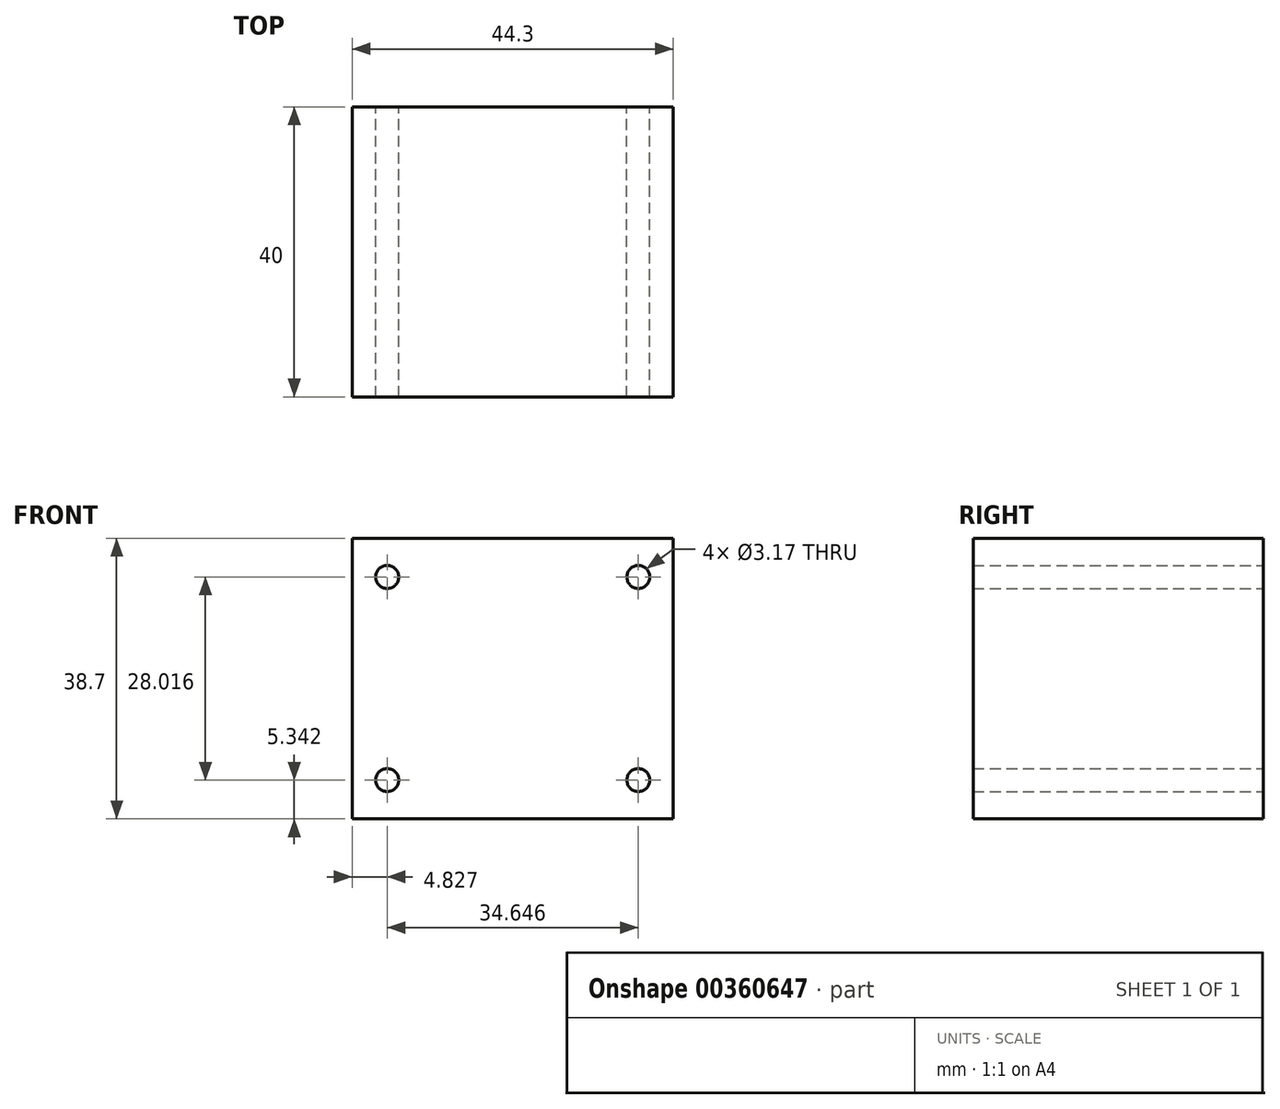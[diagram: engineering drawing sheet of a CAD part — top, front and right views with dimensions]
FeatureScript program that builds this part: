
annotation { "Feature Type Name" : "Feature", "Feature Type Description" : "" }
export const myFeature = defineFeature(function(context is Context, id is Id, definition is map)
    precondition{}
    {
        {
            var Q0;
            Q0=qCreatedBy(makeId("Front.planeOp"),FACE);
            var sketch = newSketch(context, id + "F0", { "sketchPlane" : qUnion([Q0])});
            skLineSegment(sketch, "E0.bottom", {"start": v(-22.15, 19.35) * mm, "end": v(22.15, 19.35) * mm});
            skLineSegment(sketch, "E0.top", {"start": v(-22.15, -19.35) * mm, "end": v(22.15, -19.35) * mm});
            skLineSegment(sketch, "E0.left", {"start": v(-22.15, 19.35) * mm, "end": v(-22.15, -19.35) * mm});
            skLineSegment(sketch, "E0.right", {"start": v(22.15, 19.35) * mm, "end": v(22.15, -19.35) * mm});
            skPoint(sketch, "E1", {"position": v(0, 19.35) * mm});
            skPoint(sketch, "E2", {"position": v(22.15, 0) * mm});
            skLineSegment(sketch, "E3.bottom", {"start": v(-17.32, 14) * mm, "end": v(17.32, 14) * mm, "construction": true});
            skLineSegment(sketch, "E3.top", {"start": v(-17.32, -14) * mm, "end": v(17.32, -14) * mm, "construction": true});
            skLineSegment(sketch, "E3.left", {"start": v(-17.32, 14) * mm, "end": v(-17.32, -14) * mm, "construction": true});
            skLineSegment(sketch, "E3.right", {"start": v(17.32, 14) * mm, "end": v(17.32, -14) * mm, "construction": true});
            skPoint(sketch, "E4", {"position": v(0, 14) * mm});
            skPoint(sketch, "E5", {"position": v(-17.32, 0) * mm});
            skCircle(sketch, "E6", {"center": v(-17.32, 14) * mm, "radius": 1.59 * mm});
            skCircle(sketch, "E7", {"center": v(17.32, 14) * mm, "radius": 1.59 * mm});
            skCircle(sketch, "E8", {"center": v(17.32, -14) * mm, "radius": 1.59 * mm});
            skCircle(sketch, "E9", {"center": v(-17.32, -14) * mm, "radius": 1.59 * mm});
            skSolve(sketch);
        }
        {
            var Q0;
            Q0 = qSketchRegion(id + "F0", true);
            extrude(context, id + "F1", {"entities" : qUnion([Q0]), "depth" : 40 * mm});
        }
    });
